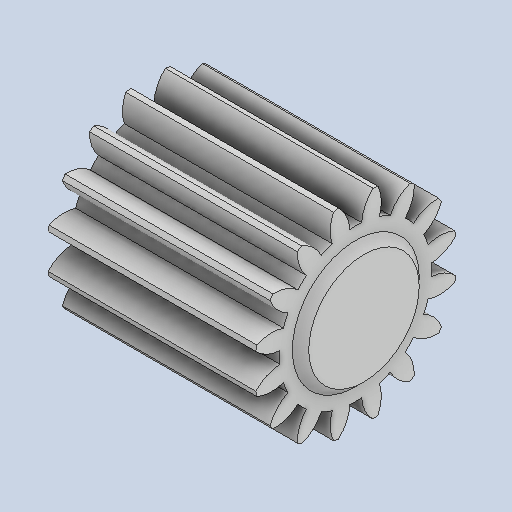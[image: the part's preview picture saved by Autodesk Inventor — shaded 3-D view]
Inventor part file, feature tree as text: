
AUTODESK INVENTOR PART (.ipt)
format: ipt  version: 2023 (Build 270158030, 158C)  size: 216,576 bytes
history: native  units: in
note: dims shown in document units (in); Inventor stores cm internally (conversion verified against a paired STEP export)
features: chamfer x1
ambient origin geometry x8: Origin, YZ Plane, XZ Plane, XY Plane, X Axis, Y Axis, Z Axis, Center Point
bodies: Solid1 (feature_tree)
feature tree (1):
  chamfer  "Chamfer1"  [1 undecoded]
note: 1 required parameter value undecoded (feature->parameter linkage not recoverable at this tier; creation-order binding heuristic only, values carry confidence <= 0.55)
